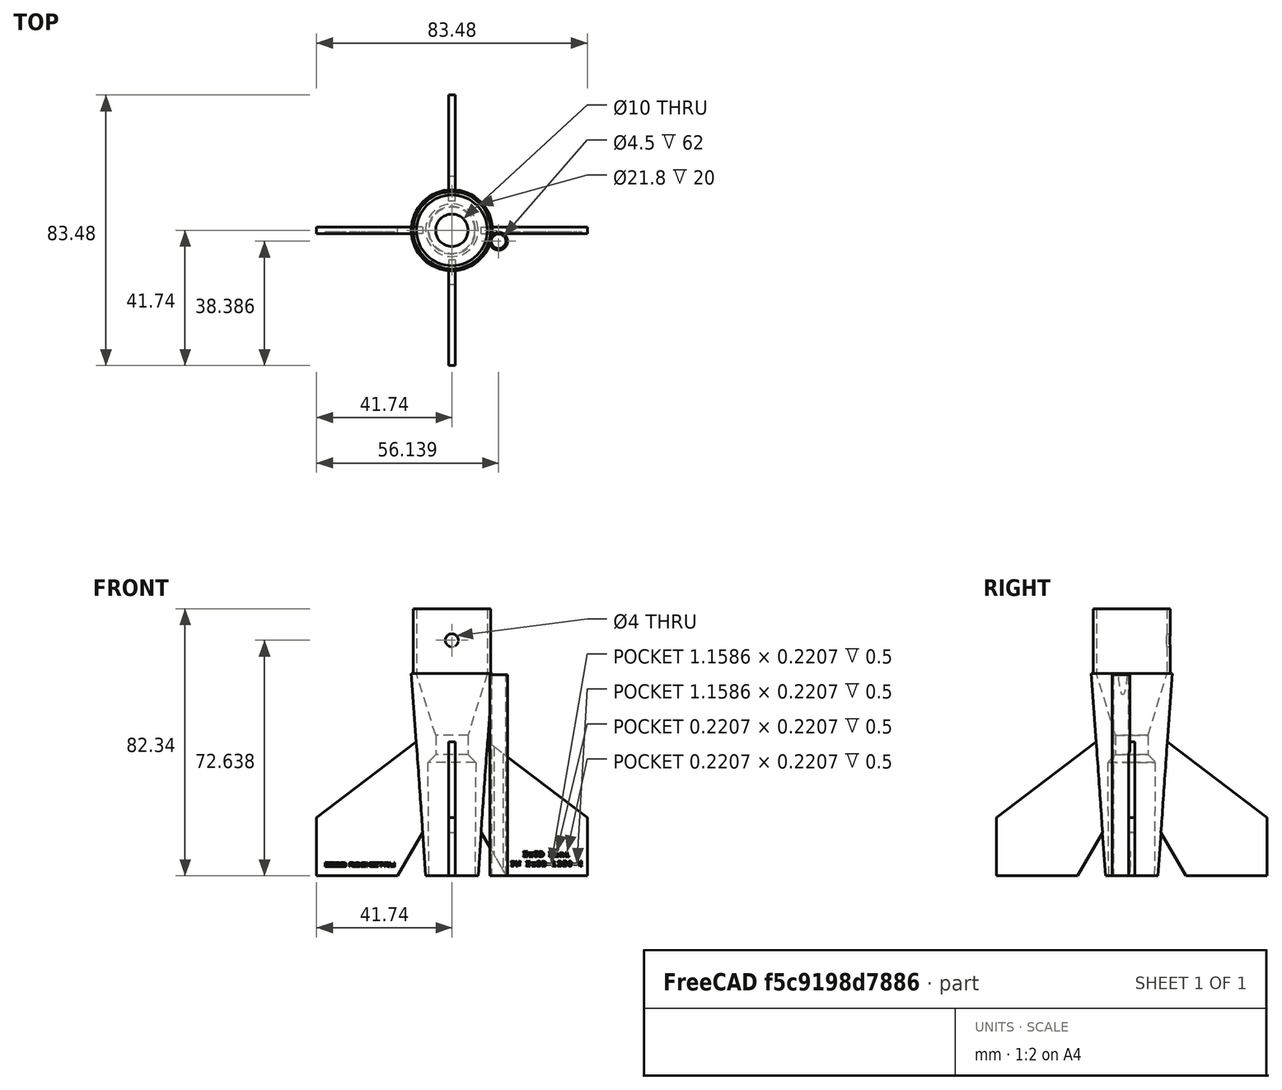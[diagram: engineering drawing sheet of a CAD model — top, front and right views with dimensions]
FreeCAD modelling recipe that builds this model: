
FCSTD DOCUMENT  (FreeCAD 0.20R29603 (Git))
Label: Ez3D-Mini-FinCan
License: All rights reserved
LicenseURL: http://en.wikipedia.org/wiki/All_rights_reserved
objects: Sketcher::SketchObject×4, Part::Part2DObjectPython×3, PartDesign::Pocket×3, PartDesign::Pad×2, PartDesign::Revolution×1, PartDesign::PolarPattern×1, PartDesign::Plane×1, PartDesign::Hole×1, Mesh::Feature×1, PartDesign::Body×1
note: 24 computed .brp shape members not serialized (recipe doc carries the construction recipe); baked Part::Feature solids carry a one-line shape summary decoded from their .brp

FEATURE [Sketcher::SketchObject] Sketch  label="Fin Can and Transition"
  FullyConstrained = true
  MapMode = 5
  Placement = pos=(0,0,0) rot=(1,0,0;1.5708rad)
  Support = -> [XZ_Plane]
  sketch-geometry (10):
    g0: LineSegment StartX=7.1 StartY=0 StartZ=0 EndX=8.1 EndY=0 EndZ=0
    g1: LineSegment StartX=8.1 StartY=0 StartZ=0 EndX=12.5 EndY=62.343 EndZ=0
    g2: LineSegment StartX=5 StartY=43.343 StartZ=0 EndX=5 EndY=37.343 EndZ=0
    g3: LineSegment StartX=5 StartY=37.343 StartZ=0 EndX=7.343 EndY=35 EndZ=0
    g4: LineSegment StartX=7.343 StartY=35 StartZ=0 EndX=7.1 EndY=0 EndZ=0
    g5: LineSegment StartX=10.9 StartY=82.343 StartZ=0 EndX=10.9 EndY=62.343 EndZ=0
    g6: LineSegment StartX=10.9 StartY=62.343 StartZ=0 EndX=5 EndY=43.343 EndZ=0
    g7: LineSegment StartX=12.5 StartY=62.343 StartZ=0 EndX=11.9 EndY=62.343 EndZ=0
    g8: LineSegment StartX=11.9 StartY=62.343 StartZ=0 EndX=11.9 EndY=82.343 EndZ=0
    g9: LineSegment StartX=11.9 StartY=82.343 StartZ=0 EndX=10.9 EndY=82.343 EndZ=0
  constraints (30):
    c: PointOnObject(g0,g-1)
    c: PointOnObject(g0,g-1)
    c: Coincident(g0,g1)
    c: Vertical(g2)
    c: Coincident(g2,g3)
    c: Coincident(g3,g4)
    c: Coincident(g4,g0)
    c: DistanceX(g0,g0) = 1
    c: DistanceX(g-1,g0) = 7.1
    c: DistanceY(g0,g3) = 35
    c: Angle(g3) = -0.785398
    c: DistanceX(g-1,g2) = 5
    c: Vertical(g5)
    c: Coincident(g5,g6)
    c: Coincident(g2,g6)
    c: Coincident(g7,g8)
    c: Vertical(g8)
    c: Coincident(g8,g9)
    c: Coincident(g9,g5)
    c: Horizontal(g9)
    c: Horizontal(g7)
    c: DistanceX(g-1,g8) = 11.9
    c: DistanceX(g9,g9) = 1
    c: DistanceX(g-1,g7) = 12.5
    c: DistanceY(g2,g2) = 6
    c: DistanceY(g2,g5) = 19
    c: Horizontal(g5,g7)
    c: DistanceY(g5,g5) = 20
    c: DistanceX(g-1,g3) = 7.343
    c: Coincident(g1,g7)
FEATURE [PartDesign::Revolution] Revolution  label="Revolution for Fin Can"
  Angle = 360
  Axis = (0,-2e-16,1)
  Base = (0,0,0)
  Placement = pos=(0,0,0) rot=(1,0,0;1.5708rad)
  Profile = -> Sketch
  ReferenceAxis = -> Sketch [V_Axis]
  Reversed = true
FEATURE [Sketcher::SketchObject] Sketch001  label="Fin"
  FullyConstrained = true
  MapMode = 5
  Placement = pos=(0,0,0) rot=(1,0,0;1.5708rad)
  Support = -> [XZ_Plane]
  sketch-geometry (5):
    g0: LineSegment StartX=16.7376 StartY=0 StartZ=0 EndX=41.7376 EndY=0 EndZ=0
    g1: LineSegment StartX=41.7376 StartY=0 StartZ=0 EndX=41.7376 EndY=18 EndZ=0
    g2: LineSegment StartX=41.7376 StartY=18 StartZ=0 EndX=7.5 EndY=44 EndZ=0
    g3: LineSegment StartX=7.5 StartY=44 StartZ=0 EndX=7.5 EndY=16 EndZ=0
    g4: LineSegment StartX=7.5 StartY=16 StartZ=0 EndX=16.7376 EndY=0 EndZ=0
  constraints (15):
    c: Horizontal(g0)
    c: Coincident(g0,g1)
    c: Coincident(g1,g2)
    c: Vertical(g1)
    c: Coincident(g2,g3)
    c: Vertical(g3)
    c: Coincident(g3,g4)
    c: Coincident(g0,g4)
    c: DistanceX(g-1,g2) = 7.5
    c: Angle(g4) = -1.0472
    c: PointOnObject(g0,g-1)
    c: DistanceY(g1,g1) = 18
    c: DistanceX(g0,g0) = 25
    c: DistanceY(g3,g3) = 28
    c: DistanceY(g0,g2) = 44
FEATURE [PartDesign::Pad] Pad  label="Fin 2mm thick"
  BaseFeature = -> Revolution
  Direction = (0,-1,-2e-16)
  Length = 2
  Length2 = 100
  Midplane = true
  Placement = pos=(0,0,0) rot=(1,0,0;1.5708rad)
  Profile = -> Sketch001
  Type = 0
FEATURE [PartDesign::PolarPattern] PolarPattern  label="Add Multiple Fins"
  Angle = 360
  Axis = -> Z_Axis
  BaseFeature = -> Pad
  Occurrences = 4
  Originals = -> [Pad]
  Placement = pos=(0,0,0) rot=(1,0,0;1.5708rad)
FEATURE [Sketcher::SketchObject] Sketch002  label="Launch Lug 4mm ID 5mm OD"
  FullyConstrained = false
  MapMode = 5
  Support = -> [XY_Plane]
  sketch-geometry (2):
    g0: Circle CenterX=14.3994 CenterY=-3.35421 CenterZ=0 NormalX=0 NormalY=0 NormalZ=1 AngleXU=0 Radius=2.75
    g1: Circle CenterX=14.3994 CenterY=-3.35421 CenterZ=0 NormalX=0 NormalY=0 NormalZ=1 AngleXU=0 Radius=2.25
  constraints (3):
    c: Coincident(g1,g0)
    c: Diameter(g0) = 5.5
    c: Diameter(g1) = 4.5
FEATURE [PartDesign::Pad] Pad001  label="Launch Lug 62mm long"
  BaseFeature = -> PolarPattern
  Direction = (0,0,1)
  Length = 62
  Length2 = 100
  Placement = pos=(0,0,0) rot=(1,0,0;1.5708rad)
  Profile = -> Sketch002
  Type = 0
FEATURE [PartDesign::Plane] DatumPlane  label="DatumPlane for Recovery Harness Hole"
  Length = 102.407
  MapMode = 5
  Placement = pos=(0,-1,1e-16) rot=(1,0,0;1.5708rad)
  ResizeMode = 0
  Support = -> [Pad001]
  Width = 126.275
FEATURE [Sketcher::SketchObject] Sketch003  label="Recovery Harness Hole"
  FullyConstrained = false
  MapMode = 5
  Placement = pos=(0,-1,1e-16) rot=(1,0,0;1.5708rad)
  Support = -> [DatumPlane]
  sketch-geometry (1):
    g0: Circle CenterX=0 CenterY=72.6377 CenterZ=0 NormalX=0 NormalY=0 NormalZ=1 AngleXU=0 Radius=1.56488
  constraints (1):
    c: PointOnObject(g0,g-2)
FEATURE [PartDesign::Hole] Hole  label="4mm hole for recovery harness"
  BaseFeature = -> Pad001
  CustomThreadClearance = 0
  Depth = 25
  DepthType = 0
  Diameter = 4
  DrillForDepth = false
  DrillPoint = 1
  DrillPointAngle = 118
  HoleCutCountersinkAngle = 90
  HoleCutCustomValues = false
  HoleCutDepth = 0
  HoleCutDiameter = 6.1
  HoleCutType = 0
  ModelThread = false
  Placement = pos=(0,0,0) rot=(1,0,0;1.5708rad)
  Profile = -> Sketch003
  Tapered = false
  TaperedAngle = 90
  ThreadClass = 0
  ThreadDepth = 25
  ThreadDepthType = 0
  ThreadDirection = 0
  ThreadFit = 0
  ThreadSize = 0
  ThreadType = 0
  Threaded = false
  UseCustomThreadClearance = false
FEATURE [Mesh::Feature] _3mmThread20x2_5_5mmTall  label="13mmThread20x2.5-5mmTall"
FEATURE [Part::Part2DObjectPython] ShapeString001  label="Marketing Name"  # Draft 2D object (typed FeaturePython)
  FontFile = <path>
  MakeFace = true
  Placement = pos=(22,-1,5.943) rot=(1,0,0;1.5708rad)
  Size = 2
  String = Ez3D Mini
  Tracking = 0
FEATURE [Part::Part2DObjectPython] ShapeString002  label="PN"  # Draft 2D object (typed FeaturePython)
  FontFile = <path>
  MakeFace = true
  Placement = pos=(18,-1,2.913) rot=(1,0,0;1.5708rad)
  Size = 2
  String = PN Ez3D-1350-4
  Tracking = 0
FEATURE [Part::Part2DObjectPython] ShapeString  label="Logo"  # Draft 2D object (typed FeaturePython)
  FontFile = <path>
  MakeFace = true
  Placement = pos=(-39.215,-1,2.796) rot=(1,0,0;1.5708rad)
  Size = 0.7
  String = Ez3D Rocketry
  Tracking = 0
FEATURE [PartDesign::Pocket] Pocket
  BaseFeature = -> Hole
  Direction = (0,1,0)
  Length = 0.5
  Length2 = 5
  Placement = pos=(0,0,0) rot=(1,0,0;1.5708rad)
  Profile = -> ShapeString001
  ReferenceAxis = -> ShapeString001 [N_Axis]
  Type = 0
FEATURE [PartDesign::Pocket] Pocket001
  BaseFeature = -> Pocket
  Direction = (0,1,0)
  Length = 0.5
  Length2 = 5
  Placement = pos=(0,0,0) rot=(1,0,0;1.5708rad)
  Profile = -> ShapeString
  ReferenceAxis = -> ShapeString [N_Axis]
  Type = 0
FEATURE [PartDesign::Pocket] Pocket002
  BaseFeature = -> Pocket001
  Direction = (0,1,0)
  Length = 0.5
  Length2 = 5
  Placement = pos=(0,0,0) rot=(1,0,0;1.5708rad)
  Profile = -> ShapeString002
  ReferenceAxis = -> ShapeString002 [N_Axis]
  Type = 0
FEATURE [PartDesign::Body] Body
  Group = -> [Sketch,Revolution,Sketch001,Pad,PolarPattern,Sketch002,Pad001,DatumPlane,Sketch003,Hole,ShapeString001,ShapeString002,ShapeString,Pocket,Pocket001,Pocket002]
  Origin = -> Origin
  Tip = -> Pocket002
note: 3 file-system paths scrubbed to <path> (originals preserved in the JSON sidecar)
